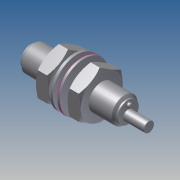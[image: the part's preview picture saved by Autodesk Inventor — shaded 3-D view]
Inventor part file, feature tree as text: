
AUTODESK INVENTOR PART (.ipt)
format: ipt  version: 2014 (Build 180170000, 170)  size: 198,656 bytes
history: native  units: in
note: dims shown in document units (in); Inventor stores cm internally (conversion verified against a paired STEP export)
features: other x1, sketch x1
ambient origin geometry x8: Origin, YZ Plane, XZ Plane, XY Plane, X Axis, Y Axis, Z Axis, Center Point
bodies: Solid1 (feature_tree)
feature tree (2):
  other  "20910-010x5000"
  sketch  "Sketch1"
